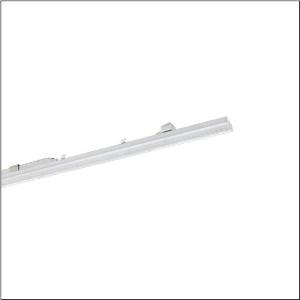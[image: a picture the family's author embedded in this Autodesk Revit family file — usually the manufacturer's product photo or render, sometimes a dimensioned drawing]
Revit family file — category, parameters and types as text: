
# Revit family: tl_l_5wd7a7d0a2c5
name_source: partatom
category: Lighting Fixtures
units: mm (PartAtom-declared; Revit-internal decimal feet)

## family parameters
Cut with Voids When Loaded = No
Host = Face
Light Source = No
Part Type = Normal
Room Calculation Point = No
Round Connector Dimension = Use Diameter
Shared = No

## types (1)
- --- (1 x LED, 9080 lm, 63.3 W, 3000K)
    Apparent Load = 63 VA
    CIE Flux Codes = 49 84 98 100 100
    Color Rendering = 80
    Color Temperature = 3000K
    Default Elevation = 1800 mm
    Description = TL L, luminaire insert, of sheet steel, galvanised, coil coated, white, length: 1.500mm, width: 66mm, height: 67mm, LED rated luminous flux: 9.080lm, light colour: 830, control gear: DALI, with terminal, 5-pole, mains connection: 230..240V, AC, 50/60Hz, rated input power: 63W, primary optical cover: cover, of PMMA, light emission: direct distribution, protection rating (complete): as luminaire, insulation class (complete): insulation class I (protective earthing), certification: CE, impact resistance: IK06, permissible ambient temperature for indoor applications: -25..+35°C, packaging unit: 1 piece
    Height = 120 mm
    Lamp = 1 x LED
    Lamp Light Flux = 9080 lm
    Lamp Power = 63.3 W
    Lamp count = 1
    Length = 1690 mm
    Luminous efficacy = 143 lm/W
    Manufacturer = Siteco
    ModVariant = No
    Model = 5WD7A7D0A2C5
    Mounting Place = Ceiling
    Mounting Type = Pendant
    Number of Poles = 1
    OnlyDefault = Yes
    Power Factor = 1
    Product Name = TL L
    Product group = luminaire insert
    ProductGroupID = 901
    Protection Class = Protection class I
    Protection Degree = Degree of protection
    RLX_Detail_Level = 1
    RLX_Emergency_Light_Flux = 0 lm
    RLX_Emergency_Type = 0
    RLX_Emergency_Type_DB = No
    RlxData = <blob elided: 17277 chars, md5=2896b8c8>
    Socket = socket
    Standby Power = 0 W
    System Light Flux = 9080 lm
    System Power = 63 W
    Type Comments = factory setting: luminous flux: 100 % | dim-lin: 254 | 420 mA
    Type Image = l_1294382.jpg
    URL = http://relux.com
    VarID = @adj_012587
    Voltage = 0 V
    Weight = 0.00 kg
    Width = 208 mm

## geometry (parser evidence)
native form markers: Blend x4, Sweep x9
no freeform markers — native parametric forms only
